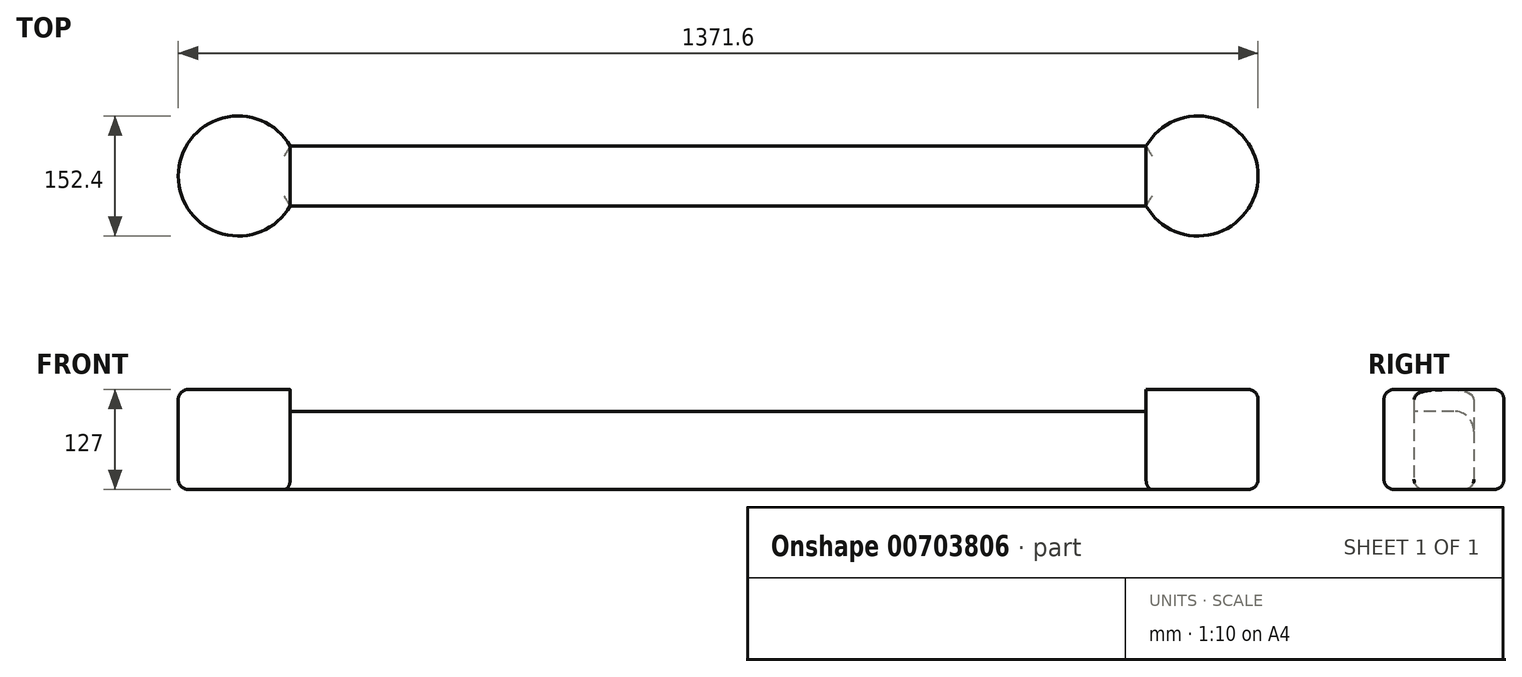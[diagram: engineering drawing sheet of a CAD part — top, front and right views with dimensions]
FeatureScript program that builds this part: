
annotation { "Feature Type Name" : "Feature", "Feature Type Description" : "" }
export const myFeature = defineFeature(function(context is Context, id is Id, definition is map)
    precondition{}
    {
        {
            var Q0;
            Q0=qCreatedBy(makeId("Top.planeOp"),FACE);
            var sketch = newSketch(context, id + "F0", { "sketchPlane" : qUnion([Q0])});
            skCircle(sketch, "E0", {"center": v(1292.6, 0) * mm, "radius": 76.2 * mm});
            skCircle(sketch, "E1", {"center": v(73.4, 0) * mm, "radius": 76.2 * mm});
            skLineSegment(sketch, "E2", {"start": v(139.45, 38) * mm, "end": v(1226.55, 38) * mm});
            skLineSegment(sketch, "E3", {"start": v(1226.55, -38) * mm, "end": v(139.45, -38) * mm});
            skLineSegment(sketch, "E4", {"start": v(139.45, 38) * mm, "end": v(139.45, -38) * mm});
            skLineSegment(sketch, "E5", {"start": v(1226.55, 38) * mm, "end": v(1226.55, -38) * mm});
            skSolve(sketch);
        }
        {
            var Q0;
            {var subQ0=sQuery(id+"F0.wireOp",EDGE,"E5");Q0=makeQuery(id+"F0.imprint","IMPRINT",FACE,{"disambiguationData":[TD([[makeQuery(id+"F0.imprint","IMPRINT",EDGE,{"derivedFrom":subQ0}),1.0]])]});}
            var Q1;
            {var subQ0=sQuery(id+"F0.wireOp",EDGE,"E4");Q1=makeQuery(id+"F0.imprint","IMPRINT",FACE,{"disambiguationData":[TD([[makeQuery(id+"F0.imprint","IMPRINT",EDGE,{"derivedFrom":subQ0}),-1.0]])]});}
            var Q2;
            Q2 = qSketchRegion(id + "F0", true);
            extrude(context, id + "F1", {"entities" : qUnion([Q0, Q1, Q2]), "depth" : 127 * mm, "offsetDistance" : 25.4 * mm});
        }
        {
            var Q0;
            Q0=makeQuery(id+"F1.opExtrude","SWEPT_FACE",FACE,{"disambiguationData":[OSD([sQuery(id+"F0.wireOp",EDGE,"E3")])]});
            var sketch = newSketch(context, id + "F2", { "sketchPlane" : qUnion([Q0])});
            skLineSegment(sketch, "E6", {"start": v(139.45, 127) * mm, "end": v(139.45, 99.36) * mm});
            skLineSegment(sketch, "E7", {"start": v(139.45, 99.36) * mm, "end": v(320.3, 99.36) * mm});
            skLineSegment(sketch, "E8", {"start": v(320.3, 99.36) * mm, "end": v(1077.13, 99.36) * mm});
            skLineSegment(sketch, "E9", {"start": v(1077.13, 99.36) * mm, "end": v(1226.55, 99.36) * mm});
            skLineSegment(sketch, "E10", {"start": v(1226.55, 99.36) * mm, "end": v(1226.55, 127) * mm});
            skLineSegment(sketch, "E11", {"start": v(1226.55, 127) * mm, "end": v(139.45, 127) * mm});
            skSolve(sketch);
        }
        {
            var Q0;
            Q0=makeQuery(id+"F2.imprint","IMPRINT",FACE,{"disambiguationData":[TD([[makeQuery(id+"F2.imprint","IMPRINT",EDGE,{"derivedFrom":sQuery(id+"F2.wireOp",EDGE,"E6")}),1.0]])]});
            var Q1;
            Q1=sQuery(id+"F2.wireOp",EDGE,"E8");
            var Q2;
            Q2=sQuery(id+"F2.wireOp",EDGE,"E6");
            var Q3;
            Q3=sQuery(id+"F2.wireOp",EDGE,"E9");
            var Q4;
            Q4=sQuery(id+"F2.wireOp",EDGE,"E7");
            var Q5;
            Q5=sQuery(id+"F2.wireOp",EDGE,"E10");
            var Q6;
            Q6=sQuery(id+"F2.wireOp",EDGE,"E11");
            extrude(context, id + "F3", {"entities" : qUnion([Q0]), "operationType" : NewBodyOperationType.REMOVE, "surfaceEntities" : qUnion([Q1, Q2, Q3, Q4, Q5, Q6]), "oppositeDirection" : true, "depth" : 76.2 * mm, "offsetDistance" : 25.4 * mm});
        }
        {
            var Q0;
            Q0=makeQuery(id+"F3.boolean.opBoolean","COPY",EDGE,{"derivedFrom":makeQuery(id+"F3.opExtrude","CAP_EDGE",EDGE,{"disambiguationData":[OSD([sQuery(id+"F2.wireOp",EDGE,"E7"),sQuery(id+"F2.wireOp",EDGE,"E8"),sQuery(id+"F2.wireOp",EDGE,"E9")])],"isStart":true})});
            var Q1;
            Q1=makeQuery(id+"F3.boolean.opBoolean","INTERSECT",EDGE,{"derivedFrom":[makeQuery(id+"F1.opExtrude","SWEPT_FACE",FACE,{"disambiguationData":[OSD([sQuery(id+"F0.wireOp",EDGE,"E2")])]}),makeQuery(id+"F3.opExtrude","SWEPT_FACE",FACE,{"disambiguationData":[OSD([sQuery(id+"F2.wireOp",EDGE,"E7"),sQuery(id+"F2.wireOp",EDGE,"E8"),sQuery(id+"F2.wireOp",EDGE,"E9")])]})]});
            fillet(context, id + "F4", {"entities" : qUnion([Q0, Q1]), "radius" : 25.4 * mm, "tangentPropagation" : true, "allowEdgeOverflow" : false});
        }
        {
            var Q0;
            Q0=makeQuery(id+"F1.opExtrude","CAP_EDGE",EDGE,{"disambiguationData":[OSD([sQuery(id+"F0.wireOp",EDGE,"E0")])],"isStart":false});
            var Q1;
            Q1=makeQuery(id+"F1.opExtrude","CAP_EDGE",EDGE,{"disambiguationData":[OSD([sQuery(id+"F0.wireOp",EDGE,"E1")])],"isStart":false});
            var Q2;
            Q2=makeQuery(id+"F1.opExtrude","CAP_EDGE",EDGE,{"disambiguationData":[OSD([sQuery(id+"F0.wireOp",EDGE,"E1")])],"isStart":true});
            var Q3;
            Q3=makeQuery(id+"F1.opExtrude","CAP_EDGE",EDGE,{"disambiguationData":[OSD([sQuery(id+"F0.wireOp",EDGE,"E0")])],"isStart":true});
            fillet(context, id + "F5", {"entities" : qUnion([Q0, Q1, Q2, Q3]), "radius" : 12.7 * mm, "tangentPropagation" : true, "allowEdgeOverflow" : false});
        }
        {
            var Q0;
            Q0=makeQuery(id+"F1.opExtrude","CAP_EDGE",EDGE,{"disambiguationData":[OSD([sQuery(id+"F0.wireOp",EDGE,"E2")])],"isStart":true});
            var Q1;
            Q1=makeQuery(id+"F1.opExtrude","CAP_EDGE",EDGE,{"disambiguationData":[OSD([sQuery(id+"F0.wireOp",EDGE,"E3")])],"isStart":true});
            fillet(context, id + "F6", {"entities" : qUnion([Q0, Q1]), "radius" : 12.7 * mm, "tangentPropagation" : true, "allowEdgeOverflow" : false});
        }
    });
